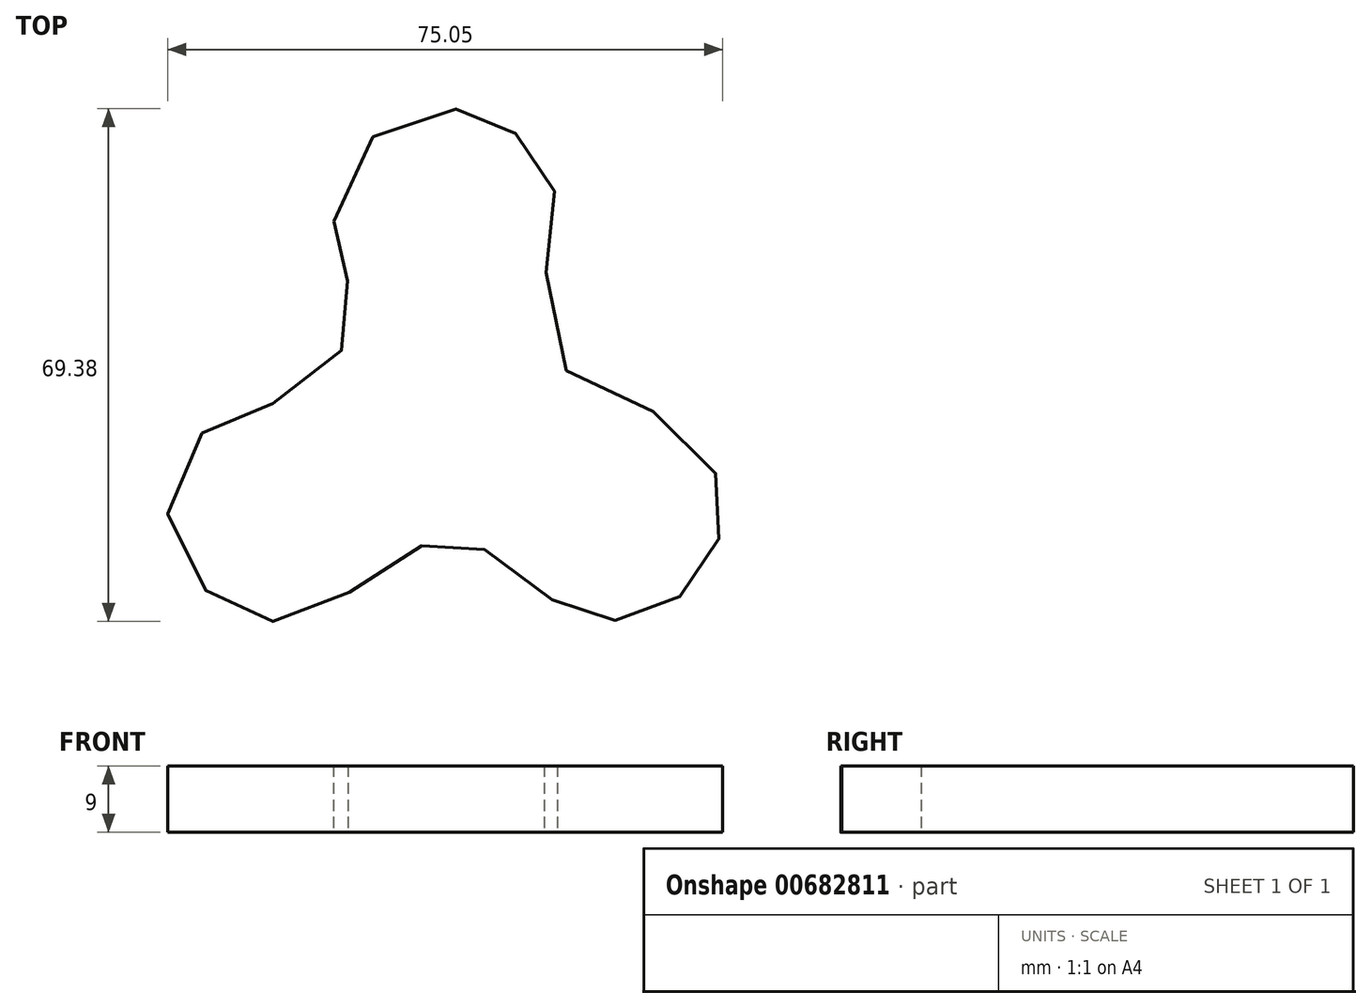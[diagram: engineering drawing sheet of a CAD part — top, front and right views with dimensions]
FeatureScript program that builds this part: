
annotation { "Feature Type Name" : "Feature", "Feature Type Description" : "" }
export const myFeature = defineFeature(function(context is Context, id is Id, definition is map)
    precondition{}
    {
        {
            var Q0;
            Q0=qCreatedBy(makeId("Top.planeOp"),FACE);
            var sketch = newSketch(context, id + "F0", { "sketchPlane" : qUnion([Q0])});
            skFitSpline(sketch, "E0", {"points": [v(-15.36, 26.24) * mm, v(-12.62, 34.8) * mm, v(-3.8, 40.96) * mm, v(2.35, 41.3) * mm, v(5.52, 40.28) * mm, v(10.91, 36.85) * mm, v(13.65, 33.09) * mm, v(14.85, 26.07) * mm, v(13.3, 18.7) * mm, v(15.15, 7.3) * mm, v(23.07, 2.16) * mm, v(32.44, -1.93) * mm, v(36.66, -8.93) * mm, v(37.21, -13.67) * mm, v(36.36, -17.92) * mm, v(33.6, -22.6) * mm, v(29.14, -26) * mm, v(24.46, -27.6) * mm, v(18.2, -27.28) * mm, v(14.68, -25.36) * mm, v(8.73, -20.47) * mm, v(3.2, -17.4) * mm, v(0, -17.07) * mm, v(-7, -18.99) * mm, v(-13.38, -24.09) * mm, v(-18.9, -27.49) * mm, v(-28.26, -27.06) * mm, v(-32.08, -24.3) * mm, v(-36.71, -18.54) * mm, v(-37.24, -9.03) * mm, v(-33.02, -2.3) * mm, v(-28.26, 0) * mm, v(-20.08, 3.37) * mm, v(-14.4, 8.65) * mm, v(-13.53, 11.32) * mm, v(-13.53, 18.97) * mm, v(-14.38, 24.07) * mm, v(-15.36, 26.24) * mm]});
            skSolve(sketch);
        }
        {
            var Q0;
            Q0=makeQuery(id+"F0.imprint","IMPRINT",FACE,{"disambiguationData":[TD([[makeQuery(id+"F0.imprint","IMPRINT",EDGE,{"derivedFrom":sQuery(id+"F0.wireOp",EDGE,"E0")}),-1.0]])]});
            extrude(context, id + "F1", {"entities" : qUnion([Q0]), "depth" : 9 * mm, "offsetDistance" : 25 * mm});
        }
    });
